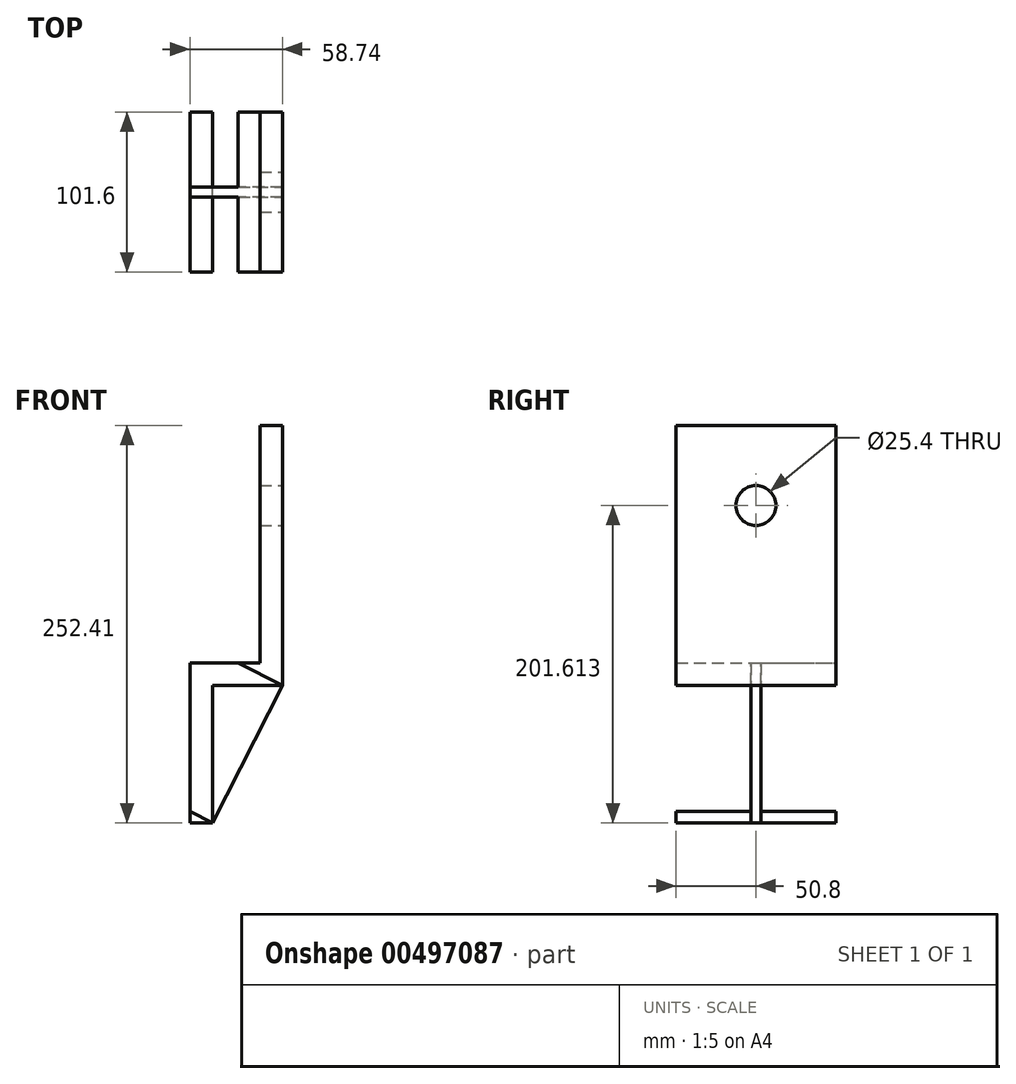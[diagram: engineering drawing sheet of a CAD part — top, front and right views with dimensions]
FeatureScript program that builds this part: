
annotation { "Feature Type Name" : "Feature", "Feature Type Description" : "" }
export const myFeature = defineFeature(function(context is Context, id is Id, definition is map)
    precondition{}
    {
        {
            var Q0;
            Q0=qCreatedBy(makeId("Front.planeOp"),FACE);
            var sketch = newSketch(context, id + "F0", { "sketchPlane" : qUnion([Q0])});
            skLineSegment(sketch, "E0", {"start": v(-37.87, -94.04) * mm, "end": v(-37.87, 7.56) * mm});
            skLineSegment(sketch, "E1", {"start": v(-37.87, 7.56) * mm, "end": v(6.58, 7.56) * mm});
            skLineSegment(sketch, "E2", {"start": v(6.58, 7.56) * mm, "end": v(6.58, 158.37) * mm});
            skLineSegment(sketch, "E3.0", {"start": v(20.87, -6.73) * mm, "end": v(20.87, 158.37) * mm});
            skLineSegment(sketch, "E3.1", {"start": v(-23.58, -6.73) * mm, "end": v(20.87, -6.73) * mm});
            skLineSegment(sketch, "E3.2", {"start": v(-23.58, -94.04) * mm, "end": v(-23.58, -6.73) * mm});
            skLineSegment(sketch, "E4", {"start": v(-37.87, -94.04) * mm, "end": v(-23.58, -94.04) * mm});
            skLineSegment(sketch, "E5", {"start": v(6.58, 158.37) * mm, "end": v(20.87, 158.37) * mm});
            skSolve(sketch);
        }
        {
            var Q0;
            Q0=makeQuery(id+"F0.imprint","IMPRINT",FACE,{"disambiguationData":[TD([[makeQuery(id+"F0.imprint","IMPRINT",EDGE,{"derivedFrom":sQuery(id+"F0.wireOp",EDGE,"E0")}),-1.0]])]});
            extrude(context, id + "F1", {"entities" : qUnion([Q0]), "depth" : 101.6 * mm});
        }
        {
            var Q0;
            Q0=makeQuery(id+"F1.opExtrude","SWEPT_FACE",FACE,{"disambiguationData":[OSD([sQuery(id+"F0.wireOp",EDGE,"E3.0")])]});
            var sketch = newSketch(context, id + "F2", { "sketchPlane" : qUnion([Q0])});
            skLineSegment(sketch, "E6", {"start": v(-50.8, 158.37) * mm, "end": v(-50.8, 107.57) * mm, "construction": true});
            skPoint(sketch, "E6.endSnap0", {"position": v(-50.8, 158.37) * mm});
            skSolve(sketch);
        }
        {
            var Q0;
            Q0=sQuery(id+"F2.wireOp",VERTEX,"E6.end");
            var Q1;
            Q1=makeQuery(id+"F1.opExtrude","SWEPT_BODY",BODY,{"disambiguationData":[OSD([sQuery(id+"F0.wireOp",EDGE,"E0"),sQuery(id+"F0.wireOp",EDGE,"E1"),sQuery(id+"F0.wireOp",EDGE,"E2"),sQuery(id+"F0.wireOp",EDGE,"E3.0"),sQuery(id+"F0.wireOp",EDGE,"E3.1"),sQuery(id+"F0.wireOp",EDGE,"E3.2"),sQuery(id+"F0.wireOp",EDGE,"E4"),sQuery(id+"F0.wireOp",EDGE,"E5")])]});
            hole(context, id + "F3", {"style" : HoleStyle.SIMPLE, "endStyle" : HoleEndStyle.THROUGH, "holeDiameter" : 25.4 * mm, "isTappedThrough" : true, "tappedDepth" : 12.7 * mm, "tapClearance" : 3, "startFromSketch" : true, "locations" : qUnion([Q0]), "scope" : qUnion([Q1])});
        }
        {
            var Q0;
            Q0=makeQuery(id+"F1.opExtrude","SWEPT_FACE",FACE,{"disambiguationData":[OSD([sQuery(id+"F0.wireOp",EDGE,"E3.2")])]});
            var sketch = newSketch(context, id + "F4", { "sketchPlane" : qUnion([Q0])});
            skLineSegment(sketch, "E7.bottom", {"start": v(-101.6, -94.04) * mm, "end": v(0, -94.04) * mm});
            skLineSegment(sketch, "E7.top", {"start": v(-101.6, -6.73) * mm, "end": v(0, -6.73) * mm});
            skLineSegment(sketch, "E7.left", {"start": v(-101.6, -94.04) * mm, "end": v(-101.6, -6.73) * mm});
            skLineSegment(sketch, "E7.right", {"start": v(0, -94.04) * mm, "end": v(0, -6.73) * mm});
            skSolve(sketch);
        }
        {
            var Q0;
            Q0=qSketchRegion(id+"F4",true);
            var Q1;
            Q1=makeQuery(id+"F1.opExtrude","SWEPT_FACE",FACE,{"disambiguationData":[OSD([sQuery(id+"F0.wireOp",EDGE,"E3.0")])]});
            extrude(context, id + "F5", {"entities" : qUnion([Q0]), "endBound" : BoundingType.UP_TO_SURFACE, "endBoundEntityFace" : qUnion([Q1]), "depth" : 29.72 * mm});
        }
        {
            var Q0;
            Q0=makeQuery(id+"F5.opExtrude","SWEPT_FACE",FACE,{"disambiguationData":[OSD([sQuery(id+"F4.wireOp",EDGE,"E7.left")])]});
            var sketch = newSketch(context, id + "F6", { "sketchPlane" : qUnion([Q0])});
            skLineSegment(sketch, "E8", {"start": v(-23.58, -94.04) * mm, "end": v(20.87, -6.73) * mm});
            skSolve(sketch);
        }
        {
            var Q0;
            Q0=makeQuery(id+"F6.imprint","IMPRINT",FACE,{"disambiguationData":[TD([[makeQuery(id+"F6.imprint","IMPRINT",EDGE,{"derivedFrom":sQuery(id+"F6.wireOp",EDGE,"E8")}),-1.0]])]});
            extrude(context, id + "F7", {"entities" : qUnion([Q0]), "operationType" : NewBodyOperationType.REMOVE, "endBound" : BoundingType.THROUGH_ALL, "oppositeDirection" : true, "depth" : 25.4 * mm});
        }
        {
            var Q0;
            Q0=makeQuery(id+"F7.boolean.opBoolean","COPY",FACE,{"derivedFrom":makeQuery(id+"F7.opExtrude","SWEPT_FACE",FACE,{"disambiguationData":[OSD([sQuery(id+"F6.wireOp",EDGE,"E8")])]})});
            var sketch = newSketch(context, id + "F8", { "sketchPlane" : qUnion([Q0])});
            skLineSegment(sketch, "E9", {"start": v(-50.8, 3.47) * mm, "end": v(-50.8, -94.5) * mm, "construction": true});
            skLineSegment(sketch, "E10.0", {"start": v(-53.97, 3.47) * mm, "end": v(-53.97, -94.5) * mm});
            skLineSegment(sketch, "E11.MirrorCS", {"start": v(-47.62, 3.47) * mm, "end": v(-47.62, -94.5) * mm});
            skSolve(sketch);
        }
        {
            var Q0;
            {var subQ0=sQuery(id+"F8.wireOp",EDGE,"E11.MirrorCS");Q0=makeQuery(id+"F8.imprint","IMPRINT",FACE,{"disambiguationData":[TD([[makeQuery(id+"F8.imprint","IMPRINT",EDGE,{"derivedFrom":subQ0}),1.0]])]});}
            extrude(context, id + "F9", {"entities" : qUnion([Q0]), "operationType" : NewBodyOperationType.REMOVE, "endBound" : BoundingType.THROUGH_ALL, "oppositeDirection" : true, "depth" : 25.4 * mm});
        }
        {
            var Q0;
            {var subQ0=sQuery(id+"F8.wireOp",EDGE,"E10.0");Q0=makeQuery(id+"F8.imprint","IMPRINT",FACE,{"disambiguationData":[TD([[makeQuery(id+"F8.imprint","IMPRINT",EDGE,{"derivedFrom":subQ0}),-1.0]])]});}
            extrude(context, id + "F10", {"entities" : qUnion([Q0]), "operationType" : NewBodyOperationType.REMOVE, "endBound" : BoundingType.THROUGH_ALL, "oppositeDirection" : true, "depth" : 25.4 * mm});
        }
    });
